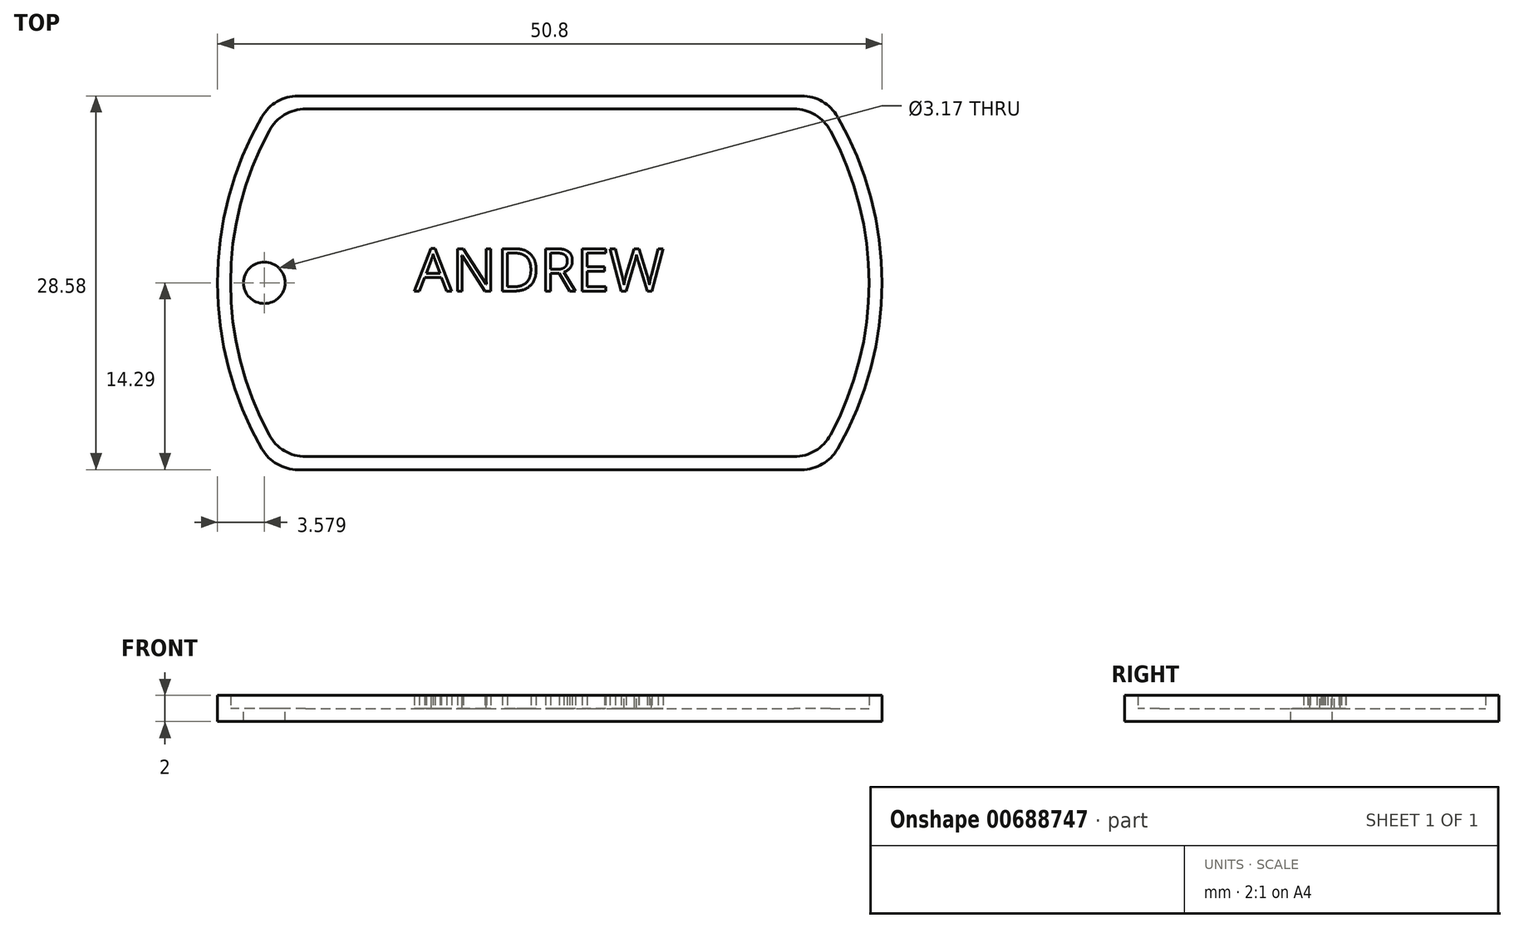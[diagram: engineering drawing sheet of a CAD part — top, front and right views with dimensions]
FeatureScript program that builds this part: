
annotation { "Feature Type Name" : "Feature", "Feature Type Description" : "" }
export const myFeature = defineFeature(function(context is Context, id is Id, definition is map)
    precondition{}
    {
        {
            var Q0;
            Q0=qCreatedBy(makeId("Top.planeOp"),FACE);
            var sketch = newSketch(context, id + "F0", { "sketchPlane" : qUnion([Q0])});
            skArc(sketch, "E0", {"start": v(-22, 12.7) * mm, "mid": v(-25.4, 0) * mm, "end": v(-22, -12.7) * mm});
            skLineSegment(sketch, "E1.top", {"start": v(-19.25, -14.29) * mm, "end": v(19.25, -14.29) * mm});
            skArc(sketch, "E2.trimOffspring", {"start": v(22, -12.7) * mm, "mid": v(25.4, 0) * mm, "end": v(22, 12.7) * mm});
            skLineSegment(sketch, "E3", {"start": v(-19.25, 14.29) * mm, "end": v(19.25, 14.29) * mm});
            skPoint(sketch, "E4.visualSharp", {"position": v(-21, 14.29) * mm});
            skArc(sketch, "E4.filletArc", {"start": v(-19.25, 14.29) * mm, "mid": v(-20.83, 13.86) * mm, "end": v(-22, 12.7) * mm});
            skPoint(sketch, "E5.visualSharp", {"position": v(21, 14.29) * mm});
            skArc(sketch, "E5.filletArc", {"start": v(22, 12.7) * mm, "mid": v(20.83, 13.86) * mm, "end": v(19.25, 14.29) * mm});
            skPoint(sketch, "E6.visualSharp", {"position": v(21, -14.29) * mm});
            skArc(sketch, "E6.filletArc", {"start": v(19.25, -14.29) * mm, "mid": v(20.83, -13.86) * mm, "end": v(22, -12.7) * mm});
            skPoint(sketch, "E7.visualSharp", {"position": v(-21, -14.29) * mm});
            skArc(sketch, "E7.filletArc", {"start": v(-22, -12.7) * mm, "mid": v(-20.83, -13.86) * mm, "end": v(-19.25, -14.29) * mm});
            skSolve(sketch);
        }
        {
            var Q0;
            Q0=makeQuery(id+"F0.imprint","IMPRINT",FACE,{"disambiguationData":[TD([[makeQuery(id+"F0.imprint","IMPRINT",EDGE,{"derivedFrom":sQuery(id+"F0.wireOp",EDGE,"E0")}),1.0]])]});
            extrude(context, id + "F1", {"entities" : qUnion([Q0]), "depth" : 1 * mm, "offsetDistance" : 25.4 * mm});
        }
        {
            var Q0;
            Q0=makeQuery(id+"F1.opExtrude","CAP_FACE",FACE,{"disambiguationData":[OSD([sQuery(id+"F0.wireOp",EDGE,"E0"),sQuery(id+"F0.wireOp",EDGE,"E1.top"),sQuery(id+"F0.wireOp",EDGE,"E2.trimOffspring"),sQuery(id+"F0.wireOp",EDGE,"E3"),sQuery(id+"F0.wireOp",EDGE,"E4.filletArc"),sQuery(id+"F0.wireOp",EDGE,"E5.filletArc"),sQuery(id+"F0.wireOp",EDGE,"E6.filletArc"),sQuery(id+"F0.wireOp",EDGE,"E7.filletArc")])],"isStart":false});
            var sketch = newSketch(context, id + "F2", { "sketchPlane" : qUnion([Q0])});
            skLineSegment(sketch, "E8.0", {"start": v(-18.66, 13.29) * mm, "end": v(18.66, 13.29) * mm});
            skArc(sketch, "E8.1", {"start": v(-21.45, 11.63) * mm, "mid": v(-24.4, 0) * mm, "end": v(-21.45, -11.63) * mm});
            skLineSegment(sketch, "E8.2", {"start": v(-18.66, -13.29) * mm, "end": v(18.66, -13.29) * mm});
            skArc(sketch, "E8.3", {"start": v(21.45, -11.63) * mm, "mid": v(24.4, 0) * mm, "end": v(21.45, 11.63) * mm});
            skPoint(sketch, "E9.visualSharp", {"position": v(-20.46, 13.29) * mm});
            skArc(sketch, "E9.filletArc", {"start": v(-18.66, 13.29) * mm, "mid": v(-20.29, 12.84) * mm, "end": v(-21.45, 11.63) * mm});
            skPoint(sketch, "E10.visualSharp", {"position": v(20.46, 13.29) * mm});
            skArc(sketch, "E10.filletArc", {"start": v(21.45, 11.63) * mm, "mid": v(20.29, 12.84) * mm, "end": v(18.66, 13.29) * mm});
            skPoint(sketch, "E11.visualSharp", {"position": v(20.46, -13.29) * mm});
            skArc(sketch, "E11.filletArc", {"start": v(18.66, -13.29) * mm, "mid": v(20.29, -12.84) * mm, "end": v(21.45, -11.63) * mm});
            skPoint(sketch, "E12.visualSharp", {"position": v(-20.46, -13.29) * mm});
            skArc(sketch, "E12.filletArc", {"start": v(-21.45, -11.63) * mm, "mid": v(-20.29, -12.84) * mm, "end": v(-18.66, -13.29) * mm});
            skLineSegment(sketch, "E13.0", {"start": v(-19.25, 14.29) * mm, "end": v(19.25, 14.29) * mm});
            skArc(sketch, "E13.1", {"start": v(-22, 12.7) * mm, "mid": v(-25.4, 0) * mm, "end": v(-22, -12.7) * mm});
            skLineSegment(sketch, "E13.2", {"start": v(-19.25, -14.29) * mm, "end": v(19.25, -14.29) * mm});
            skArc(sketch, "E13.3", {"start": v(22, -12.7) * mm, "mid": v(25.4, 0) * mm, "end": v(22, 12.7) * mm});
            skPoint(sketch, "E14.visualSharp", {"position": v(-21, -14.29) * mm});
            skArc(sketch, "E14.filletArc", {"start": v(-22, -12.7) * mm, "mid": v(-20.83, -13.86) * mm, "end": v(-19.25, -14.29) * mm});
            skPoint(sketch, "E15.visualSharp", {"position": v(21, -14.29) * mm});
            skArc(sketch, "E15.filletArc", {"start": v(19.25, -14.29) * mm, "mid": v(20.83, -13.86) * mm, "end": v(22, -12.7) * mm});
            skPoint(sketch, "E16.visualSharp", {"position": v(21, 14.29) * mm});
            skArc(sketch, "E16.filletArc", {"start": v(22, 12.7) * mm, "mid": v(20.83, 13.86) * mm, "end": v(19.25, 14.29) * mm});
            skPoint(sketch, "E17.visualSharp", {"position": v(-21, 14.29) * mm});
            skArc(sketch, "E17.filletArc", {"start": v(-19.25, 14.29) * mm, "mid": v(-20.83, 13.86) * mm, "end": v(-22, 12.7) * mm});
            skSolve(sketch);
        }
        {
            var Q0;
            Q0=makeQuery(id+"F2.imprint","IMPRINT",FACE,{"disambiguationData":[TD([[makeQuery(id+"F2.imprint","IMPRINT",EDGE,{"derivedFrom":sQuery(id+"F2.wireOp",EDGE,"E8.0")}),1.0]])]});
            extrude(context, id + "F3", {"entities" : qUnion([Q0]), "operationType" : NewBodyOperationType.ADD, "depth" : 1 * mm, "offsetDistance" : 25.4 * mm});
        }
        {
            var Q0;
            Q0=makeQuery(id+"F1.opExtrude","CAP_FACE",FACE,{"disambiguationData":[OSD([sQuery(id+"F0.wireOp",EDGE,"E0"),sQuery(id+"F0.wireOp",EDGE,"E1.top"),sQuery(id+"F0.wireOp",EDGE,"E2.trimOffspring"),sQuery(id+"F0.wireOp",EDGE,"E3"),sQuery(id+"F0.wireOp",EDGE,"E4.filletArc"),sQuery(id+"F0.wireOp",EDGE,"E5.filletArc"),sQuery(id+"F0.wireOp",EDGE,"E6.filletArc"),sQuery(id+"F0.wireOp",EDGE,"E7.filletArc")])],"isStart":false});
            var sketch = newSketch(context, id + "F4", { "sketchPlane" : qUnion([Q0])});
            skCircle(sketch, "E18", {"center": v(-21.82, 0) * mm, "radius": 1.59 * mm});
            skSolve(sketch);
        }
        {
            var Q0;
            Q0=makeQuery(id+"F4.imprint","IMPRINT",FACE,{"disambiguationData":[TD([[makeQuery(id+"F4.imprint","IMPRINT",EDGE,{"derivedFrom":sQuery(id+"F4.wireOp",EDGE,"E18")}),1.0]])]});
            extrude(context, id + "F5", {"entities" : qUnion([Q0]), "operationType" : NewBodyOperationType.REMOVE, "oppositeDirection" : true, "depth" : 1 * mm, "offsetDistance" : 25.4 * mm});
        }
        {
            var Q0;
            Q0=makeQuery(id+"F1.opExtrude","CAP_FACE",FACE,{"disambiguationData":[OSD([sQuery(id+"F0.wireOp",EDGE,"E0"),sQuery(id+"F0.wireOp",EDGE,"E1.top"),sQuery(id+"F0.wireOp",EDGE,"E2.trimOffspring"),sQuery(id+"F0.wireOp",EDGE,"E3"),sQuery(id+"F0.wireOp",EDGE,"E4.filletArc"),sQuery(id+"F0.wireOp",EDGE,"E5.filletArc"),sQuery(id+"F0.wireOp",EDGE,"E6.filletArc"),sQuery(id+"F0.wireOp",EDGE,"E7.filletArc")])],"isStart":false});
            var sketch = newSketch(context, id + "F6", { "sketchPlane" : qUnion([Q0])});
            skText(sketch, "E19", { "text": "ANDREW", "fontName": "OpenSans-Regular.ttf"});
            const initialGuessF6  = {"E19": [-0.01035, -0.00063, 1, 0, 0.00326]};
            skSetInitialGuess(sketch, initialGuessF6);
            skSolve(sketch);
        }
        {
            var Q0;
            Q0 = qSketchRegion(id + "F6", true);
            extrude(context, id + "F7", {"entities" : qUnion([Q0]), "operationType" : NewBodyOperationType.ADD, "depth" : 1 * mm, "offsetDistance" : 25.4 * mm});
        }
    });
